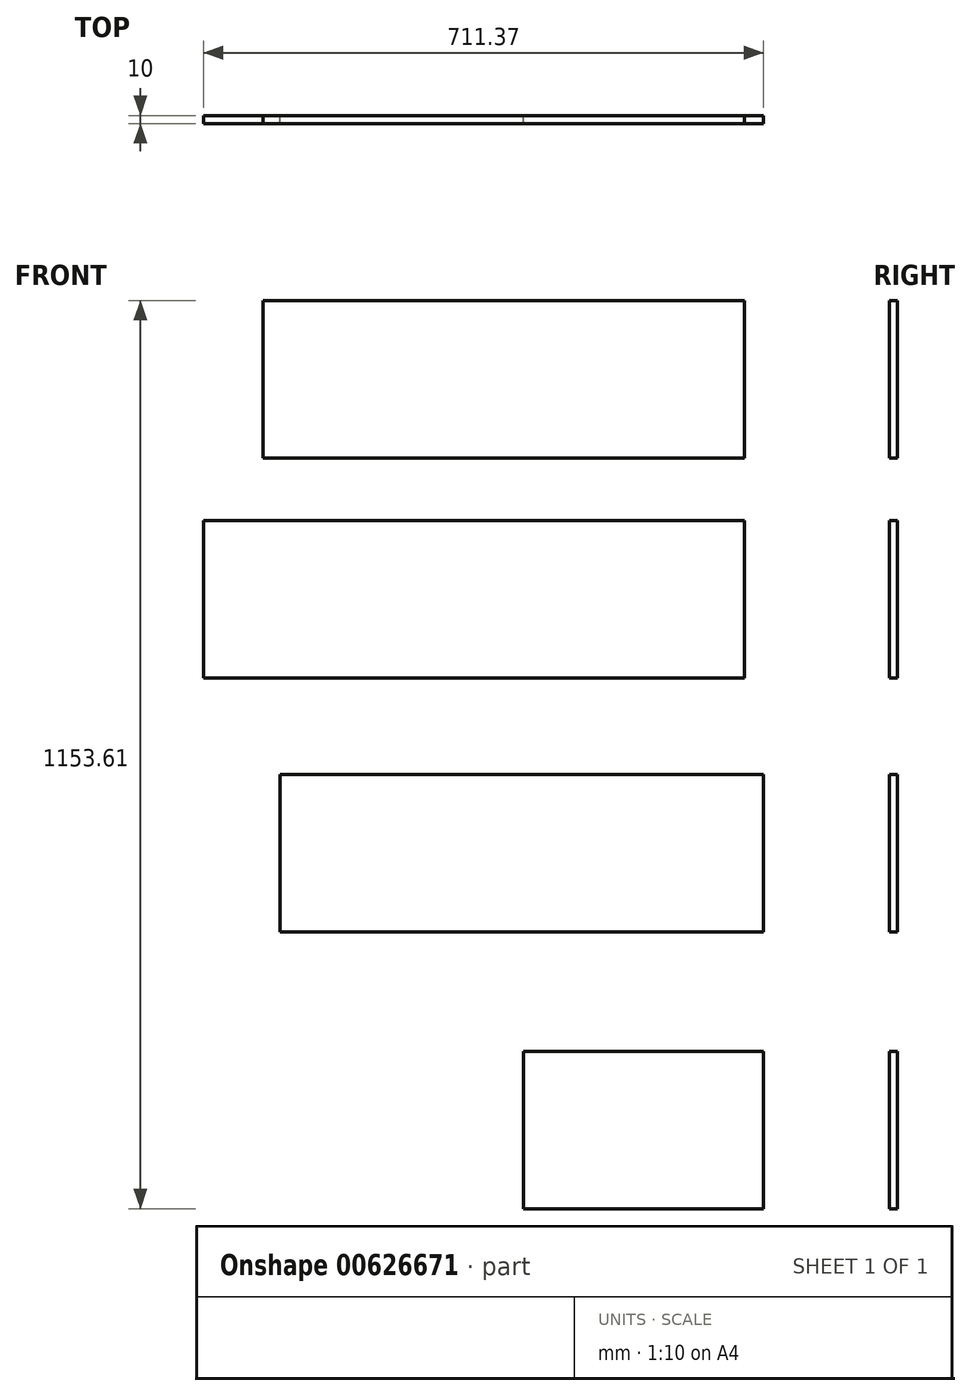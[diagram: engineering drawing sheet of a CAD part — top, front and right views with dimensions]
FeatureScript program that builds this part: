
annotation { "Feature Type Name" : "Feature", "Feature Type Description" : "" }
export const myFeature = defineFeature(function(context is Context, id is Id, definition is map)
    precondition{}
    {
        {
            var Q0;
            Q0=qCreatedBy(makeId("Front.planeOp"),FACE);
            var sketch = newSketch(context, id + "F0", { "sketchPlane" : qUnion([Q0])});
            skLineSegment(sketch, "E0.bottom", {"start": v(-635.37, 279.72) * mm, "end": v(-24.37, 279.72) * mm});
            skLineSegment(sketch, "E0.top", {"start": v(-635.37, 79.72) * mm, "end": v(-24.37, 79.72) * mm});
            skLineSegment(sketch, "E0.left", {"start": v(-635.37, 279.72) * mm, "end": v(-635.37, 79.72) * mm});
            skLineSegment(sketch, "E0.right", {"start": v(-24.37, 279.72) * mm, "end": v(-24.37, 79.72) * mm});
            skLineSegment(sketch, "E1.bottom", {"start": v(-711.37, 0) * mm, "end": v(-24.37, 0) * mm});
            skLineSegment(sketch, "E1.top", {"start": v(-711.37, -200) * mm, "end": v(-24.37, -200) * mm});
            skLineSegment(sketch, "E1.left", {"start": v(-711.37, 0) * mm, "end": v(-711.37, -200) * mm});
            skLineSegment(sketch, "E1.right", {"start": v(-24.37, 0) * mm, "end": v(-24.37, -200) * mm});
            skLineSegment(sketch, "E2.bottom", {"start": v(-614, -322.4) * mm, "end": v(0, -322.4) * mm});
            skLineSegment(sketch, "E2.top", {"start": v(-614, -522.4) * mm, "end": v(0, -522.4) * mm});
            skLineSegment(sketch, "E2.left", {"start": v(-614, -322.4) * mm, "end": v(-614, -522.4) * mm});
            skLineSegment(sketch, "E2.right", {"start": v(0, -322.4) * mm, "end": v(0, -522.4) * mm});
            skLineSegment(sketch, "E3.bottom", {"start": v(-305, -673.9) * mm, "end": v(0, -673.9) * mm});
            skLineSegment(sketch, "E3.top", {"start": v(-305, -873.9) * mm, "end": v(0, -873.9) * mm});
            skLineSegment(sketch, "E3.left", {"start": v(-305, -673.9) * mm, "end": v(-305, -873.9) * mm});
            skLineSegment(sketch, "E3.right", {"start": v(0, -673.9) * mm, "end": v(0, -873.9) * mm});
            skSolve(sketch);
        }
        {
            var Q0;
            Q0 = qSketchRegion(id + "F0", true);
            extrude(context, id + "F1", {"entities" : qUnion([Q0]), "depth" : 10 * mm, "offsetDistance" : 25 * mm});
        }
    });
